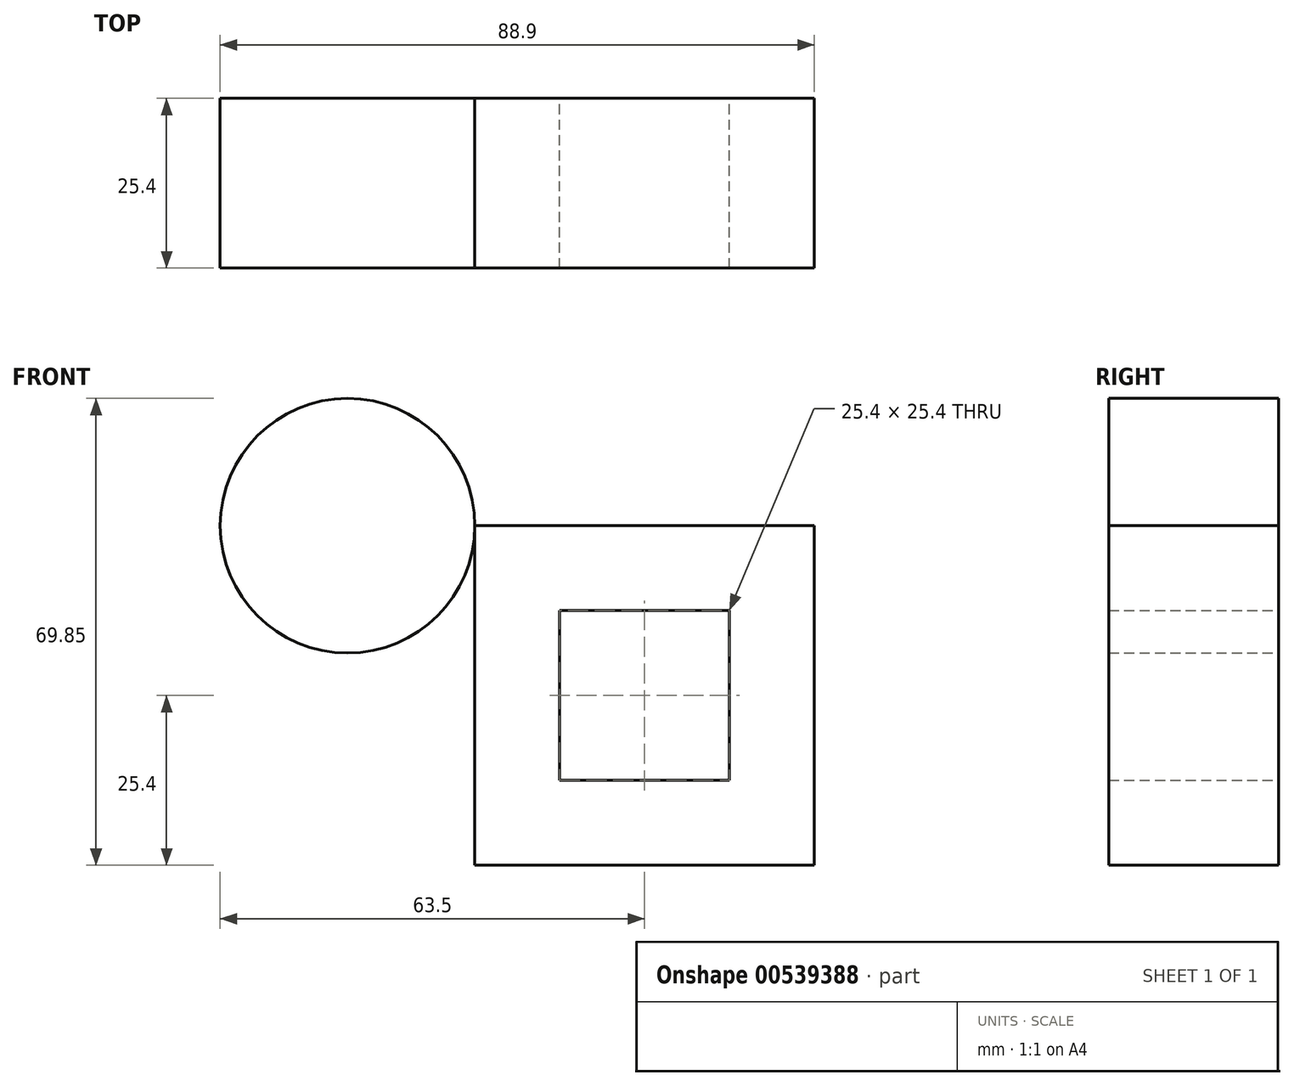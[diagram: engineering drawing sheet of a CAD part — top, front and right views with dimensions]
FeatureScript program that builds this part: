
annotation { "Feature Type Name" : "Feature", "Feature Type Description" : "" }
export const myFeature = defineFeature(function(context is Context, id is Id, definition is map)
    precondition{}
    {
        {
            var Q0;
            Q0=qCreatedBy(makeId("Front.planeOp"),FACE);
            var sketch = newSketch(context, id + "F0", { "sketchPlane" : qUnion([Q0])});
            skLineSegment(sketch, "E0", {"start": v(-50.8, 50.8) * mm, "end": v(-50.8, 0) * mm});
            skLineSegment(sketch, "E1", {"start": v(0, 50.8) * mm, "end": v(0, 0) * mm});
            skLineSegment(sketch, "E2", {"start": v(-50.8, 50.8) * mm, "end": v(0, 50.8) * mm});
            skLineSegment(sketch, "E3", {"start": v(0, 0) * mm, "end": v(-50.8, 0) * mm});
            skCircle(sketch, "E4", {"center": v(-69.85, 50.8) * mm, "radius": 19.05 * mm});
            skLineSegment(sketch, "E5", {"start": v(-50.8, 50.8) * mm, "end": v(0, 0) * mm, "construction": true});
            skLineSegment(sketch, "E6.bottom", {"start": v(-38.1, 38.1) * mm, "end": v(-12.7, 38.1) * mm});
            skLineSegment(sketch, "E6.top", {"start": v(-38.1, 12.7) * mm, "end": v(-12.7, 12.7) * mm});
            skLineSegment(sketch, "E6.left", {"start": v(-38.1, 38.1) * mm, "end": v(-38.1, 12.7) * mm});
            skLineSegment(sketch, "E6.right", {"start": v(-12.7, 38.1) * mm, "end": v(-12.7, 12.7) * mm});
            skLineSegment(sketch, "E7", {"start": v(0, 50.8) * mm, "end": v(-50.8, 0) * mm, "construction": true});
            skSolve(sketch);
        }
        {
            var Q0;
            Q0=makeQuery(id+"F0.imprint","IMPRINT",FACE,{"disambiguationData":[TD([[makeQuery(id+"F0.imprint","IMPRINT",EDGE,{"derivedFrom":sQuery(id+"F0.wireOp",EDGE,"E0")}),1.0]])]});
            var Q1;
            Q1=makeQuery(id+"F0.imprint","IMPRINT",FACE,{"disambiguationData":[TD([[makeQuery(id+"F0.imprint","IMPRINT",EDGE,{"derivedFrom":sQuery(id+"F0.wireOp",EDGE,"E4")}),1.0]])]});
            extrude(context, id + "F1", {"entities" : qUnion([Q0, Q1]), "depth" : 25.4 * mm, "offsetDistance" : 25.4 * mm});
        }
    });
